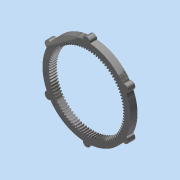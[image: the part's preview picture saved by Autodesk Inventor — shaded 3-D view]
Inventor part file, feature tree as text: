
AUTODESK INVENTOR PART (.ipt)
format: ipt  version: 2015 (Build 190159000, 159)  size: 505,344 bytes
history: native  units: in
note: dims shown in document units (in); Inventor stores cm internally (conversion verified against a paired STEP export)
features: pattern_circular x2, extrude x2, sketch x2, other x1, direct_edit x1, imported_body x1, move_body x1
ambient origin geometry x8: Origin, YZ Plane, XZ Plane, XY Plane, X Axis, Y Axis, Z Axis, Center Point
bodies: Solid1 (feature_tree)
feature tree (10):
  other  "a_1b10-n480961"
  direct_edit  "Direct Edit1"
  pattern_circular  "Circular Pattern1"  Count=48 Angle=360.0deg
  extrude  "Extrusion1"  TaperAngle=0.0deg  [1 undecoded]
  extrude  "Extrusion2"  Depth=1.0in
  pattern_circular  "Circular Pattern2"  [2 undecoded]
  imported_body  "Base1"
  sketch  "Sketch1"  dims[d0=0.0in d1=0.0in d2=0.0625in d3=18.8976in d4=360.0deg]
  sketch  "Sketch2"  dims[d6=2.3622in d7=0.0in d8=0.0in d9=0.1969in d10=1.0in d11=0.0in d12=2.3622in d13=360.0deg]
  move_body  "Move1"
note: 3 required parameter values undecoded (feature->parameter linkage not recoverable at this tier; creation-order binding heuristic only, values carry confidence <= 0.55)
